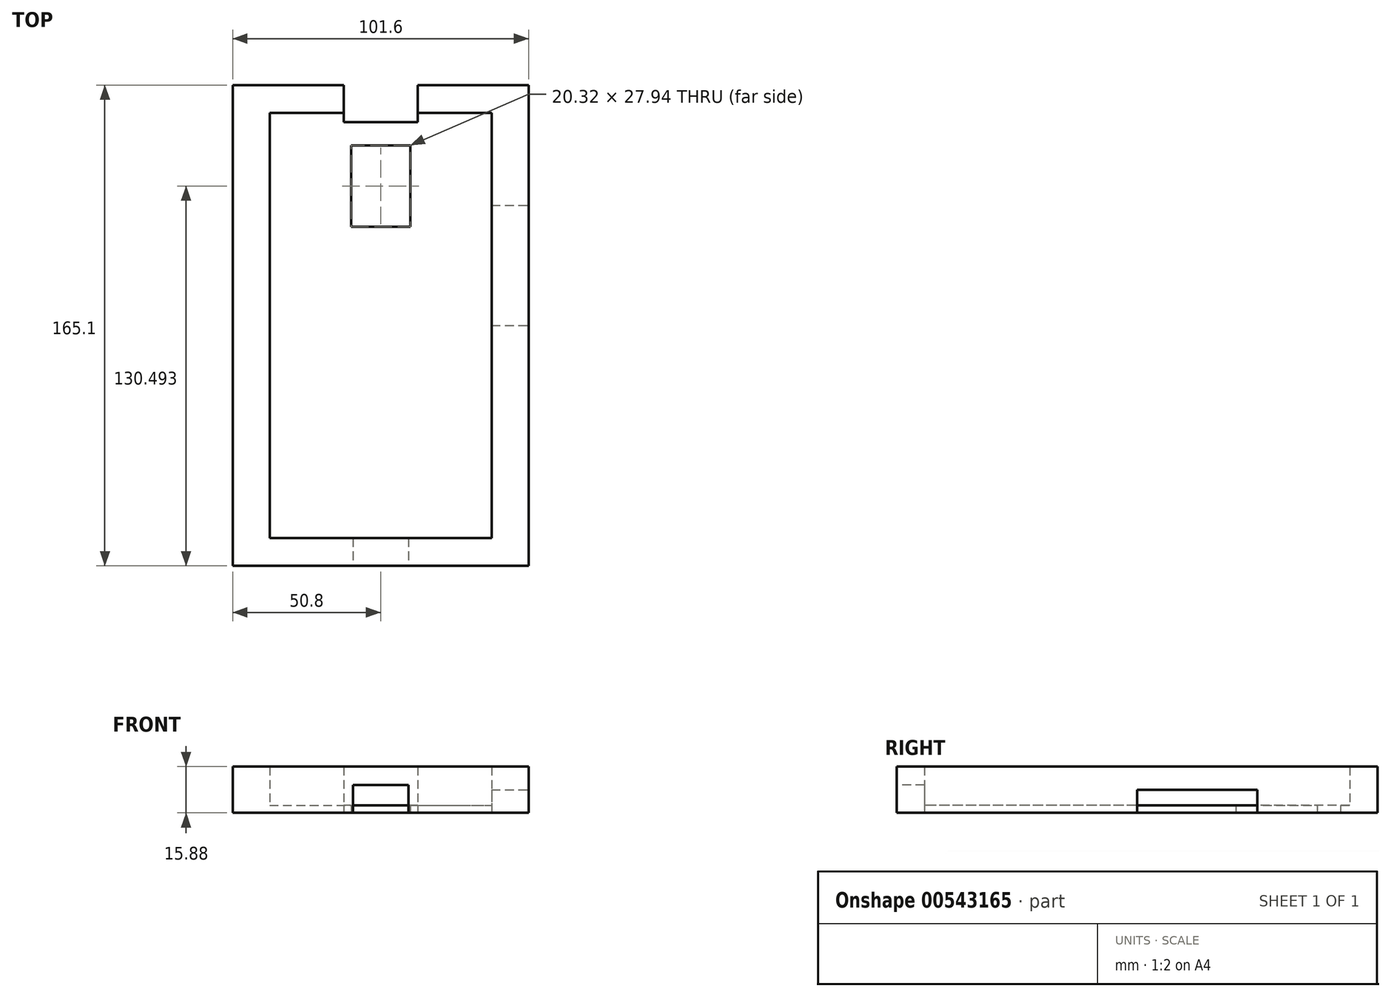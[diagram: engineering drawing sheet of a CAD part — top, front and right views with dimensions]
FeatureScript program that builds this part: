
annotation { "Feature Type Name" : "Feature", "Feature Type Description" : "" }
export const myFeature = defineFeature(function(context is Context, id is Id, definition is map)
    precondition{}
    {
        {
            var Q0;
            Q0=qCreatedBy(makeId("Top.planeOp"),FACE);
            var sketch = newSketch(context, id + "F0", { "sketchPlane" : qUnion([Q0])});
            skLineSegment(sketch, "E0.bottom", {"start": v(50.8, 82.55) * mm, "end": v(-50.8, 82.55) * mm});
            skLineSegment(sketch, "E0.top", {"start": v(50.8, -82.55) * mm, "end": v(-50.8, -82.55) * mm});
            skLineSegment(sketch, "E0.left", {"start": v(50.8, 82.55) * mm, "end": v(50.8, -82.55) * mm});
            skLineSegment(sketch, "E0.right", {"start": v(-50.8, 82.55) * mm, "end": v(-50.8, -82.55) * mm});
            skPoint(sketch, "E0.middle", {"position": v(0, 0) * mm});
            skLineSegment(sketch, "E1", {"start": v(-38.1, 82.55) * mm, "end": v(-38.1, -82.55) * mm});
            skLineSegment(sketch, "E2", {"start": v(38.1, 82.55) * mm, "end": v(38.1, -82.55) * mm});
            skLineSegment(sketch, "E3", {"start": v(-50.8, 73.03) * mm, "end": v(50.8, 73.03) * mm});
            skLineSegment(sketch, "E4", {"start": v(-50.8, -73.03) * mm, "end": v(50.8, -73.03) * mm});
            skSolve(sketch);
        }
        {
            var Q0;
            {var subQ0=sQuery(id+"F0.wireOp",EDGE,"E0.left");var subQ1=sQuery(id+"F0.wireOp",EDGE,"E0.bottom");var subQ2=makeQuery(id+"F0.imprint","INTERSECT",VERTEX,{"derivedFrom":[subQ1,subQ0]});Q0=makeQuery(id+"F0.imprint","IMPRINT",FACE,{"disambiguationData":[TD([[makeQuery(id+"F0.imprint","IMPRINT",EDGE,{"disambiguationData":[TD([[subQ2,-1.0]])],"derivedFrom":subQ1}),1.0]])]});}
            var Q1;
            {var subQ0=sQuery(id+"F0.wireOp",EDGE,"E0.right");var subQ1=sQuery(id+"F0.wireOp",EDGE,"E0.bottom");var subQ2=makeQuery(id+"F0.imprint","INTERSECT",VERTEX,{"derivedFrom":[subQ1,subQ0]});Q1=makeQuery(id+"F0.imprint","IMPRINT",FACE,{"disambiguationData":[TD([[makeQuery(id+"F0.imprint","IMPRINT",EDGE,{"disambiguationData":[TD([[subQ2,1.0]])],"derivedFrom":subQ1}),1.0]])]});}
            var Q2;
            {var subQ0=sQuery(id+"F0.wireOp",EDGE,"E0.left");var subQ1=sQuery(id+"F0.wireOp",EDGE,"E0.top");var subQ2=makeQuery(id+"F0.imprint","INTERSECT",VERTEX,{"derivedFrom":[subQ1,subQ0]});Q2=makeQuery(id+"F0.imprint","IMPRINT",FACE,{"disambiguationData":[TD([[makeQuery(id+"F0.imprint","IMPRINT",EDGE,{"disambiguationData":[TD([[subQ2,-1.0]])],"derivedFrom":subQ1}),-1.0]])]});}
            var Q3;
            {var subQ0=sQuery(id+"F0.wireOp",EDGE,"E1");var subQ1=sQuery(id+"F0.wireOp",EDGE,"E0.top");var subQ2=makeQuery(id+"F0.imprint","INTERSECT",VERTEX,{"derivedFrom":[subQ1,subQ0]});Q3=makeQuery(id+"F0.imprint","IMPRINT",FACE,{"disambiguationData":[TD([[makeQuery(id+"F0.imprint","IMPRINT",EDGE,{"disambiguationData":[TD([[subQ2,1.0]])],"derivedFrom":subQ1}),-1.0]])]});}
            var Q4;
            {var subQ0=sQuery(id+"F0.wireOp",EDGE,"E3");var subQ1=sQuery(id+"F0.wireOp",EDGE,"E0.left");var subQ2=makeQuery(id+"F0.imprint","INTERSECT",VERTEX,{"derivedFrom":[subQ1,subQ0]});Q4=makeQuery(id+"F0.imprint","IMPRINT",FACE,{"disambiguationData":[TD([[makeQuery(id+"F0.imprint","IMPRINT",EDGE,{"disambiguationData":[TD([[subQ2,-1.0]])],"derivedFrom":subQ1}),-1.0]])]});}
            var Q5;
            {var subQ0=sQuery(id+"F0.wireOp",EDGE,"E0.right");var subQ1=sQuery(id+"F0.wireOp",EDGE,"E0.top");var subQ2=makeQuery(id+"F0.imprint","INTERSECT",VERTEX,{"derivedFrom":[subQ1,subQ0]});Q5=makeQuery(id+"F0.imprint","IMPRINT",FACE,{"disambiguationData":[TD([[makeQuery(id+"F0.imprint","IMPRINT",EDGE,{"disambiguationData":[TD([[subQ2,1.0]])],"derivedFrom":subQ1}),-1.0]])]});}
            var Q6;
            {var subQ0=sQuery(id+"F0.wireOp",EDGE,"E3");var subQ1=sQuery(id+"F0.wireOp",EDGE,"E0.right");var subQ2=makeQuery(id+"F0.imprint","INTERSECT",VERTEX,{"derivedFrom":[subQ1,subQ0]});Q6=makeQuery(id+"F0.imprint","IMPRINT",FACE,{"disambiguationData":[TD([[makeQuery(id+"F0.imprint","IMPRINT",EDGE,{"disambiguationData":[TD([[subQ2,-1.0]])],"derivedFrom":subQ1}),1.0]])]});}
            var Q7;
            {var subQ0=sQuery(id+"F0.wireOp",EDGE,"E1");var subQ1=sQuery(id+"F0.wireOp",EDGE,"E0.bottom");var subQ2=makeQuery(id+"F0.imprint","INTERSECT",VERTEX,{"derivedFrom":[subQ1,subQ0]});Q7=makeQuery(id+"F0.imprint","IMPRINT",FACE,{"disambiguationData":[TD([[makeQuery(id+"F0.imprint","IMPRINT",EDGE,{"disambiguationData":[TD([[subQ2,1.0]])],"derivedFrom":subQ1}),1.0]])]});}
            extrude(context, id + "F1", {"entities" : qUnion([Q0, Q1, Q2, Q3, Q4, Q5, Q6, Q7]), "depth" : 15.88 * mm, "offsetDistance" : 25.4 * mm});
        }
        {
            var Q0;
            {var subQ0=sQuery(id+"F0.wireOp",EDGE,"E3");var subQ1=sQuery(id+"F0.wireOp",EDGE,"E1");var subQ2=makeQuery(id+"F0.imprint","INTERSECT",VERTEX,{"derivedFrom":[subQ1,subQ0]});Q0=makeQuery(id+"F0.imprint","IMPRINT",FACE,{"disambiguationData":[TD([[makeQuery(id+"F0.imprint","IMPRINT",EDGE,{"disambiguationData":[TD([[subQ2,-1.0]])],"derivedFrom":subQ1}),1.0]])]});}
            extrude(context, id + "F2", {"entities" : qUnion([Q0]), "operationType" : NewBodyOperationType.ADD, "depth" : 2.54 * mm, "offsetDistance" : 25.4 * mm});
        }
        {
            var Q0;
            Q0=makeQuery(id+"F1.opExtrude","SWEPT_FACE",FACE,{"disambiguationData":[OSD([sQuery(id+"F0.wireOp",EDGE,"E0.top")])]});
            var sketch = newSketch(context, id + "F3", { "sketchPlane" : qUnion([Q0])});
            skLineSegment(sketch, "E5", {"start": v(9.52, 15.88) * mm, "end": v(9.52, 0) * mm});
            skLineSegment(sketch, "E6", {"start": v(-9.53, 15.88) * mm, "end": v(-9.53, 0) * mm});
            skLineSegment(sketch, "E7", {"start": v(-50.8, 9.52) * mm, "end": v(50.8, 9.53) * mm});
            skSolve(sketch);
        }
        {
            var Q0;
            {var subQ0=sQuery(id+"F3.wireOp",EDGE,"E5");var subQ1=makeQuery(id+"F1.opExtrude","CAP_EDGE",EDGE,{"disambiguationData":[OSD([sQuery(id+"F0.wireOp",EDGE,"E0.top")])],"isStart":true});var subQ2=makeQuery(id+"F3.imprint","INTERSECT",VERTEX,{"derivedFrom":[subQ1,subQ0]});Q0=makeQuery(id+"F3.imprint","IMPRINT",FACE,{"disambiguationData":[TD([[makeQuery(id+"F3.imprint","IMPRINT",EDGE,{"disambiguationData":[TD([[subQ2,1.0]])],"derivedFrom":subQ0}),-1.0]])]});}
            extrude(context, id + "F4", {"entities" : qUnion([Q0]), "operationType" : NewBodyOperationType.REMOVE, "oppositeDirection" : true, "depth" : 9.52 * mm, "offsetDistance" : 25.4 * mm});
        }
        {
            var Q0;
            Q0=makeQuery(id+"F1.opExtrude","SWEPT_FACE",FACE,{"disambiguationData":[OSD([sQuery(id+"F0.wireOp",EDGE,"E0.left")])]});
            var sketch = newSketch(context, id + "F5", { "sketchPlane" : qUnion([Q0])});
            skLineSegment(sketch, "E8", {"start": v(41.28, 15.88) * mm, "end": v(41.28, 0) * mm});
            skPoint(sketch, "E8.endSnap0", {"position": v(0, 0) * mm});
            skLineSegment(sketch, "E9", {"start": v(-82.55, 7.94) * mm, "end": v(82.55, 7.94) * mm});
            skLineSegment(sketch, "E10", {"start": v(0, 15.88) * mm, "end": v(0, 0) * mm});
            skLineSegment(sketch, "E11", {"start": v(73.03, 15.88) * mm, "end": v(73.03, 0) * mm});
            skSolve(sketch);
        }
        {
            var Q0;
            {var subQ0=sQuery(id+"F5.wireOp",EDGE,"E8");var subQ1=makeQuery(id+"F1.opExtrude","CAP_EDGE",EDGE,{"disambiguationData":[OSD([sQuery(id+"F0.wireOp",EDGE,"E0.left")])],"isStart":true});var subQ2=makeQuery(id+"F5.imprint","INTERSECT",VERTEX,{"derivedFrom":[subQ1,subQ0]});Q0=makeQuery(id+"F5.imprint","IMPRINT",FACE,{"disambiguationData":[TD([[makeQuery(id+"F5.imprint","IMPRINT",EDGE,{"disambiguationData":[TD([[subQ2,1.0]])],"derivedFrom":subQ0}),-1.0]])]});}
            extrude(context, id + "F6", {"entities" : qUnion([Q0]), "operationType" : NewBodyOperationType.REMOVE, "oppositeDirection" : true, "depth" : 12.7 * mm, "offsetDistance" : 25.4 * mm});
        }
        {
            var Q0;
            {var subQ0=sQuery(id+"F0.wireOp",EDGE,"E4");var subQ1=sQuery(id+"F0.wireOp",EDGE,"E3");var subQ2=sQuery(id+"F0.wireOp",EDGE,"E2");var subQ3=sQuery(id+"F0.wireOp",EDGE,"E1");Q0=makeQuery(id+"F2.boolean.opBoolean","MERGE",FACE,{"derivedFrom":[makeQuery(id+"F1.opExtrude","CAP_FACE",FACE,{"disambiguationData":[OSD([sQuery(id+"F0.wireOp",EDGE,"E0.bottom"),sQuery(id+"F0.wireOp",EDGE,"E0.top"),sQuery(id+"F0.wireOp",EDGE,"E0.left"),sQuery(id+"F0.wireOp",EDGE,"E0.right"),subQ3,subQ2,subQ1,subQ0])],"isStart":true}),makeQuery(id+"F2.opExtrude","CAP_FACE",FACE,{"disambiguationData":[OSD([subQ3,subQ2,subQ1,subQ0])],"isStart":true})]});}
            var sketch = newSketch(context, id + "F7", { "sketchPlane" : qUnion([Q0])});
            skLineSegment(sketch, "E12", {"start": v(50.8, -61.91) * mm, "end": v(-50.8, -61.91) * mm});
            skLineSegment(sketch, "E13", {"start": v(50.8, -33.97) * mm, "end": v(-50.8, -33.97) * mm});
            skLineSegment(sketch, "E14", {"start": v(10.16, -61.91) * mm, "end": v(10.16, -33.97) * mm});
            skLineSegment(sketch, "E15", {"start": v(-10.16, -61.91) * mm, "end": v(-10.16, -33.97) * mm});
            skSolve(sketch);
        }
        {
            var Q0;
            Q0 = qSketchRegion(id + "F7", true);
            extrude(context, id + "F8", {"entities" : qUnion([Q0]), "operationType" : NewBodyOperationType.REMOVE, "oppositeDirection" : true, "depth" : 25.4 * mm, "offsetDistance" : 25.4 * mm});
        }
        {
            var Q0;
            Q0=makeQuery(id+"F1.opExtrude","SWEPT_FACE",FACE,{"disambiguationData":[OSD([sQuery(id+"F0.wireOp",EDGE,"E0.bottom")])]});
            var sketch = newSketch(context, id + "F9", { "sketchPlane" : qUnion([Q0])});
            skLineSegment(sketch, "E16", {"start": v(-12.7, 15.88) * mm, "end": v(-12.7, 0) * mm});
            skLineSegment(sketch, "E17", {"start": v(12.7, 15.88) * mm, "end": v(12.7, 0) * mm});
            skLineSegment(sketch, "E18", {"start": v(-38.1, 15.88) * mm, "end": v(-38.1, 0) * mm});
            skLineSegment(sketch, "E19", {"start": v(38.1, 15.88) * mm, "end": v(38.1, 0) * mm});
            skSolve(sketch);
        }
        {
            var Q0;
            Q0 = qSketchRegion(id + "F9", true);
            var Q1;
            {var subQ0=sQuery(id+"F9.wireOp",EDGE,"E16");Q1=makeQuery(id+"F9.imprint","IMPRINT",FACE,{"disambiguationData":[TD([[makeQuery(id+"F9.imprint","IMPRINT",EDGE,{"derivedFrom":subQ0}),1.0]])]});}
            extrude(context, id + "F10", {"entities" : qUnion([Q0, Q1]), "operationType" : NewBodyOperationType.REMOVE, "oppositeDirection" : true, "depth" : 12.7 * mm, "offsetDistance" : 25.4 * mm});
        }
    });
